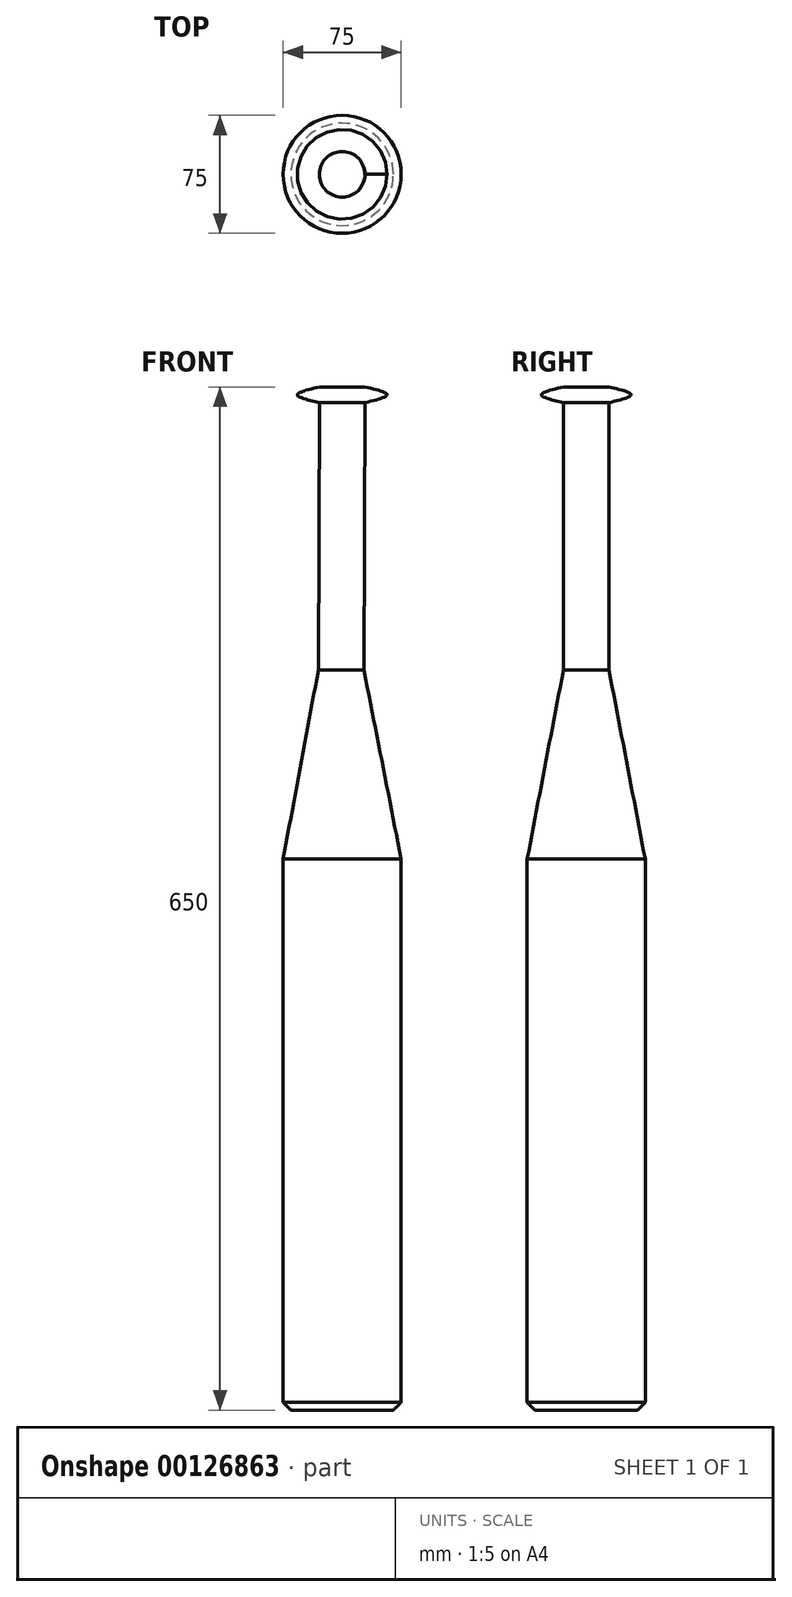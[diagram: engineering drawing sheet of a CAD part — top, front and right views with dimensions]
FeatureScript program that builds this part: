
annotation { "Feature Type Name" : "Feature", "Feature Type Description" : "" }
export const myFeature = defineFeature(function(context is Context, id is Id, definition is map)
    precondition{}
    {
        {
            var Q0;
            Q0=qCreatedBy(makeId("Top.planeOp"),FACE);
            cPlane(context, id + "F0", {"entities" : qUnion([Q0]), "cplaneType" : CPlaneType.OFFSET, "offset" : 300 * mm, "width" : 152.4 * mm, "height" : 152.4 * mm});
        }
        {
            var Q0;
            Q0=qCreatedBy(makeId("Top.planeOp"),FACE);
            cPlane(context, id + "F1", {"entities" : qUnion([Q0]), "cplaneType" : CPlaneType.OFFSET, "offset" : 295 * mm, "width" : 150 * mm, "height" : 150 * mm});
        }
        {
            var Q0;
            Q0=qCreatedBy(makeId("Top.planeOp"),FACE);
            cPlane(context, id + "F2", {"entities" : qUnion([Q0]), "cplaneType" : CPlaneType.OFFSET, "offset" : 290 * mm, "width" : 150 * mm, "height" : 150 * mm});
        }
        {
            var Q0;
            Q0=qCreatedBy(makeId("Top.planeOp"),FACE);
            cPlane(context, id + "F3", {"entities" : qUnion([Q0]), "cplaneType" : CPlaneType.OFFSET, "offset" : 350 * mm, "oppositeDirection" : true, "width" : 150 * mm, "height" : 150 * mm});
        }
        {
            var Q0;
            Q0=qCreatedBy(id+"F3.planeOp",FACE);
            cPlane(context, id + "F4", {"entities" : qUnion([Q0]), "cplaneType" : CPlaneType.OFFSET, "offset" : 5 * mm, "width" : 150 * mm, "height" : 150 * mm});
        }
        {
            var Q0;
            Q0=qCreatedBy(id+"F3.planeOp",FACE);
            var sketch = newSketch(context, id + "F5", { "sketchPlane" : qUnion([Q0])});
            skCircle(sketch, "E0", {"center": v(0, 0) * mm, "radius": 32.5 * mm});
            skSolve(sketch);
        }
        {
            var Q0;
            Q0=qCreatedBy(id+"F4.planeOp",FACE);
            var sketch = newSketch(context, id + "F6", { "sketchPlane" : qUnion([Q0])});
            skCircle(sketch, "E1", {"center": v(0, 0) * mm, "radius": 37.5 * mm});
            skSolve(sketch);
        }
        {
            var Q0;
            Q0 = qSketchRegion(id + "F5", true);
            var Q1;
            Q1 = qSketchRegion(id + "F6", true);
            loft(context, id + "F7", {"sheetProfilesArray" : [{ "sheetProfileEntities" : qUnion([Q0]) }, { "sheetProfileEntities" : qUnion([Q1]) }]});
        }
        {
            var Q0;
            Q0=qCreatedBy(makeId("Top.planeOp"),FACE);
            var sketch = newSketch(context, id + "F8", { "sketchPlane" : qUnion([Q0])});
            skCircle(sketch, "E2", {"center": v(0, 0) * mm, "radius": 37.5 * mm});
            skSolve(sketch);
        }
        {
            var Q1;
            Q1 = qSketchRegion(id + "F8", true);
            var Q2;
            Q2 = qSketchRegion(id + "F6", true);
            loft(context, id + "F9", {"operationType" : NewBodyOperationType.ADD, "sheetProfilesArray" : [{ "sheetProfileEntities" : qUnion([Q1]) }, { "sheetProfileEntities" : qUnion([Q2]) }]});
        }
        {
            var Q0;
            Q0=qCreatedBy(makeId("Top.planeOp"),FACE);
            cPlane(context, id + "F10", {"entities" : qUnion([Q0]), "cplaneType" : CPlaneType.OFFSET, "offset" : 120 * mm, "width" : 150 * mm, "height" : 150 * mm});
        }
        {
            var Q0;
            Q0=qCreatedBy(id+"F10.planeOp",FACE);
            var sketch = newSketch(context, id + "F11", { "sketchPlane" : qUnion([Q0])});
            skCircle(sketch, "E3", {"center": v(-0.64, 0) * mm, "radius": 14.5 * mm});
            skSolve(sketch);
        }
        {
            var Q0;
            Q0 = qSketchRegion(id + "F8", true);
            var Q1;
            Q1 = qSketchRegion(id + "F11", true);
            loft(context, id + "F12", {"sheetProfilesArray" : [{ "sheetProfileEntities" : qUnion([Q0]) }, { "sheetProfileEntities" : qUnion([Q1]) }]});
        }
        {
            var Q0;
            Q0=qCreatedBy(id+"F2.planeOp",FACE);
            var sketch = newSketch(context, id + "F13", { "sketchPlane" : qUnion([Q0])});
            skCircle(sketch, "E4", {"center": v(0, 0) * mm, "radius": 14.5 * mm});
            skSolve(sketch);
        }
        {
            var Q0;
            Q0 = qSketchRegion(id + "F11", true);
            var Q1;
            Q1 = qSketchRegion(id + "F13", true);
            loft(context, id + "F14", {"sheetProfilesArray" : [{ "sheetProfileEntities" : qUnion([Q0]) }, { "sheetProfileEntities" : qUnion([Q1]) }]});
        }
        {
            var Q0;
            Q0=qCreatedBy(id+"F1.planeOp",FACE);
            var sketch = newSketch(context, id + "F15", { "sketchPlane" : qUnion([Q0])});
            skCircle(sketch, "E5", {"center": v(0, 0) * mm, "radius": 28.5 * mm});
            skSolve(sketch);
        }
        {
            var Q0;
            Q0=qCreatedBy(id+"F0.planeOp",FACE);
            var sketch = newSketch(context, id + "F16", { "sketchPlane" : qUnion([Q0])});
            skCircle(sketch, "E6", {"center": v(0, 0) * mm, "radius": 14.5 * mm});
            skSolve(sketch);
        }
        {
            var Q0;
            Q0 = qSketchRegion(id + "F13", true);
            var Q1;
            Q1 = qSketchRegion(id + "F15", true);
            var Q2;
            Q2 = qSketchRegion(id + "F16", true);
            loft(context, id + "F17", {"sheetProfilesArray" : [{ "sheetProfileEntities" : qUnion([Q0]) }, { "sheetProfileEntities" : qUnion([Q1]) }, { "sheetProfileEntities" : qUnion([Q2]) }]});
        }
    });
